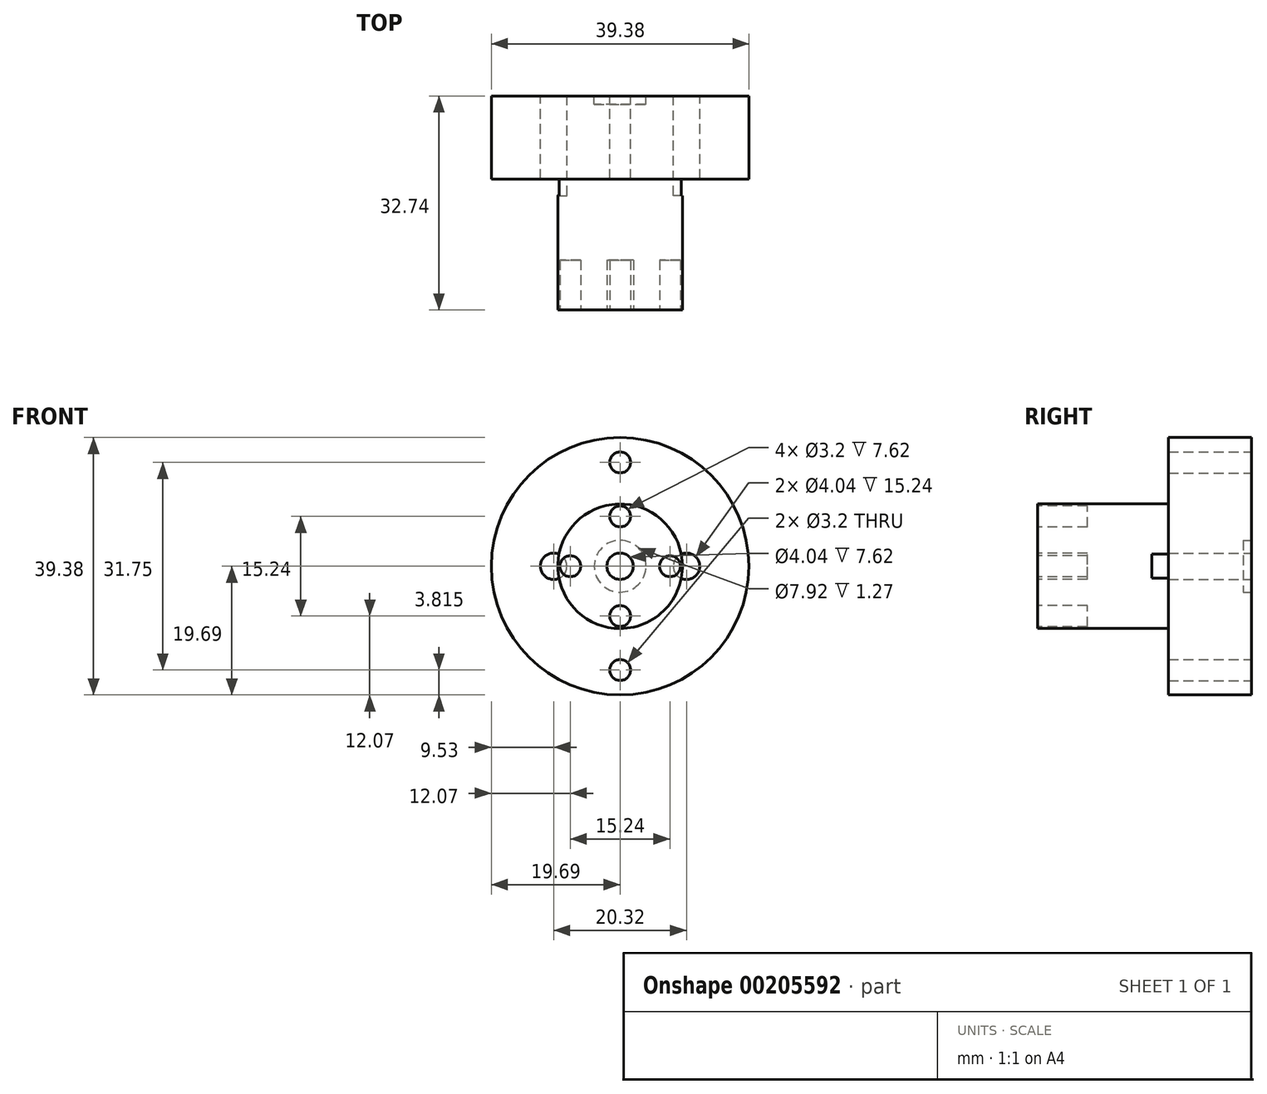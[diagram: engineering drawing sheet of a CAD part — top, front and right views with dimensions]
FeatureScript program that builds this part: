
annotation { "Feature Type Name" : "Feature", "Feature Type Description" : "" }
export const myFeature = defineFeature(function(context is Context, id is Id, definition is map)
    precondition{}
    {
        {
            var Q0;
            Q0=qCreatedBy(makeId("Front.planeOp"),FACE);
            var sketch = newSketch(context, id + "F0", { "sketchPlane" : qUnion([Q0])});
            skCircle(sketch, "E0", {"center": v(0, 0) * mm, "radius": 19.69 * mm});
            skSolve(sketch);
        }
        {
            var Q0;
            Q0=qSketchRegion(id+"F0",true);
            extrude(context, id + "F1", {"entities" : qUnion([Q0]), "depth" : 12.7 * mm});
        }
        {
            var Q0;
            Q0=makeQuery(id+"F1.opExtrude","CAP_FACE",FACE,{"disambiguationData":[OSD([sQuery(id+"F0.wireOp",EDGE,"E0")])],"isStart":false});
            var sketch = newSketch(context, id + "F2", { "sketchPlane" : qUnion([Q0])});
            skCircle(sketch, "E1", {"center": v(0, 0) * mm, "radius": 9.53 * mm});
            skSolve(sketch);
        }
        {
            var Q0;
            Q0=qSketchRegion(id+"F2",true);
            extrude(context, id + "F3", {"entities" : qUnion([Q0]), "operationType" : NewBodyOperationType.ADD, "depth" : 20.04 * mm});
        }
        {
            var Q0;
            Q0=makeQuery(id+"F3.opExtrude","CAP_FACE",FACE,{"disambiguationData":[OSD([sQuery(id+"F2.wireOp",EDGE,"E1")])],"isStart":false});
            var sketch = newSketch(context, id + "F4", { "sketchPlane" : qUnion([Q0])});
            skCircle(sketch, "E2", {"center": v(7.62, 0) * mm, "radius": 1.6 * mm});
            skCircle(sketch, "E3", {"center": v(0, 7.62) * mm, "radius": 1.6 * mm});
            skCircle(sketch, "E4", {"center": v(-7.62, 0) * mm, "radius": 1.6 * mm});
            skCircle(sketch, "E5", {"center": v(0, -7.62) * mm, "radius": 1.6 * mm});
            skCircle(sketch, "E6", {"center": v(0, 0) * mm, "radius": 2.02 * mm});
            skSolve(sketch);
        }
        {
            var Q0;
            Q0=qSketchRegion(id+"F4",true);
            extrude(context, id + "F5", {"entities" : qUnion([Q0]), "operationType" : NewBodyOperationType.REMOVE, "oppositeDirection" : true, "depth" : 7.62 * mm});
        }
        {
            var Q0;
            Q0=makeQuery(id+"F1.opExtrude","CAP_FACE",FACE,{"disambiguationData":[OSD([sQuery(id+"F0.wireOp",EDGE,"E0")])],"isStart":true});
            var sketch = newSketch(context, id + "F6", { "sketchPlane" : qUnion([Q0])});
            skCircle(sketch, "E7", {"center": v(0, 0) * mm, "radius": 3.96 * mm});
            skSolve(sketch);
        }
        {
            var Q0;
            Q0=qSketchRegion(id+"F6",true);
            extrude(context, id + "F7", {"entities" : qUnion([Q0]), "operationType" : NewBodyOperationType.REMOVE, "oppositeDirection" : true, "depth" : 1.27 * mm});
        }
        {
            var Q0;
            Q0=makeQuery(id+"F1.opExtrude","CAP_FACE",FACE,{"disambiguationData":[OSD([sQuery(id+"F0.wireOp",EDGE,"E0")])],"isStart":true});
            var sketch = newSketch(context, id + "F8", { "sketchPlane" : qUnion([Q0])});
            skCircle(sketch, "E8", {"center": v(0, 15.88) * mm, "radius": 1.6 * mm});
            skCircle(sketch, "E9", {"center": v(10.16, 0) * mm, "radius": 2.02 * mm});
            skCircle(sketch, "E10", {"center": v(0, -15.88) * mm, "radius": 1.6 * mm});
            skCircle(sketch, "E11", {"center": v(-10.16, 0) * mm, "radius": 2.02 * mm});
            skSolve(sketch);
        }
        {
            var Q0;
            Q0=qSketchRegion(id+"F8",true);
            extrude(context, id + "F9", {"entities" : qUnion([Q0]), "operationType" : NewBodyOperationType.REMOVE, "oppositeDirection" : true, "depth" : 15.24 * mm});
        }
    });
